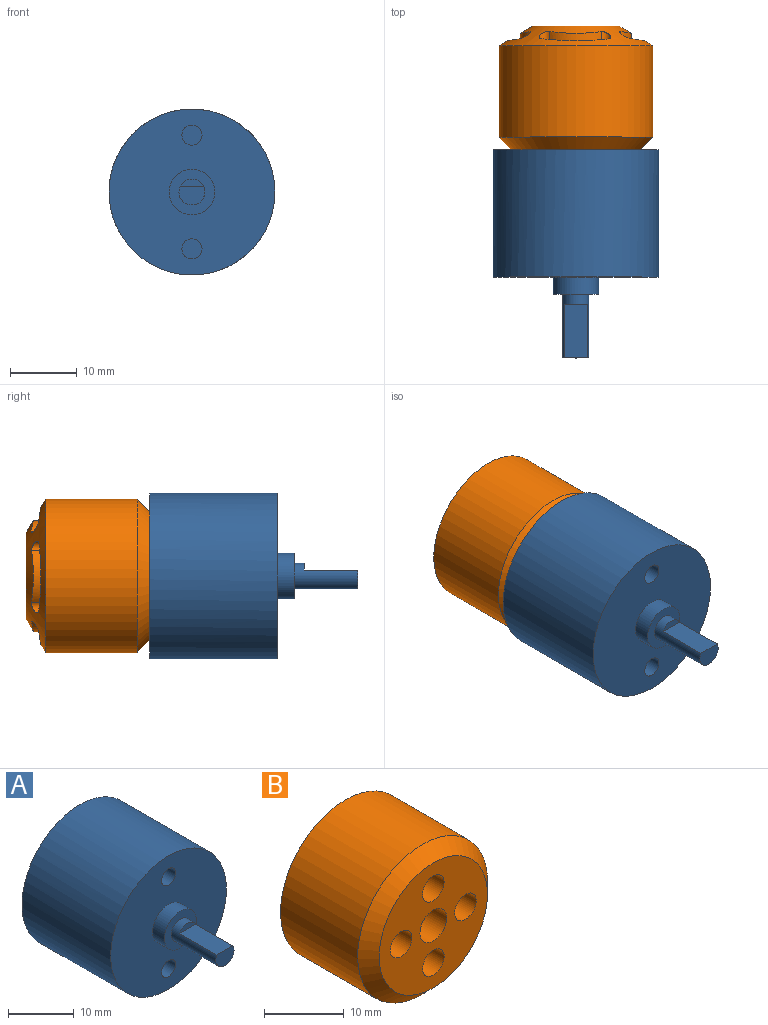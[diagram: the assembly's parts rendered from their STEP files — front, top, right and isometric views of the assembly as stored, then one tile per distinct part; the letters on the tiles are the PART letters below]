
ASSEMBLY  parts=2 mates=1
PART A: 15 faces, bbox 24.8x31.1x24.8 mm
  f0: cylinder r=12.4mm len=24.8mm, axis (0,-1,0), area 1481.6mm2, adj f2,f12
  f1: plane 6.83x6.83mm, normal (0,-1,0), area 24.8mm2, adj f3,f4
  f2: plane 24.8x24.8mm, normal (0,-1,0), area 432.3mm2, adj f0,f3,f8,f10
  f3: cylinder r=3.42mm len=6.83mm, axis (0,1,0), area 54.5mm2, adj f1,f2
  f4: cylinder r=1.94mm len=9.55mm, axis (0,1,0), area 82.5mm2, adj f1,f5,f6,f7
  f5: plane 3.88x2.84mm, normal (0,-1,0), area 9.3mm2, adj f4,f7
  f6: plane 3.44x1.05mm, normal (0,-1,0), area 2.6mm2, adj f4,f7
  f7: plane 8x3.44mm, normal (0,0,1), area 27.5mm2, adj f4,f5,f6
  f8: cylinder r=1.5mm len=4mm, axis (0,-1,0), area 37.7mm2, adj f2,f9
  f9: plane 3x3mm, normal (0,-1,0), area 7.1mm2, adj f8
  f10: cylinder r=1.5mm len=4mm, axis (0,-1,0), area 37.7mm2, adj f2,f11
  f11: plane 3x3mm, normal (0,-1,0), area 7.1mm2, adj f10
  f12: plane 24.8x24.8mm, normal (0,1,0), area 451.4mm2, adj f0,f13
  f13: cylinder r=3.17mm len=6.35mm, axis (0,1,0), area 51.2mm2, adj f12,f14
  f14: plane 6.35x6.35mm, normal (0,1,0), area 31.7mm2, adj f13
PART B: 35 faces, bbox 23x18.5x23 mm
  f0: plane 12.84x12.84mm, normal (0,1,0), area 129.5mm2, adj f24
  f1: cylinder r=11.5mm len=23mm, axis (0,-1,0), area 987.2mm2, adj f23,f24
  f2: plane 19.19x19.19mm, normal (0,-1,0), area 225.7mm2, adj f23,f25,f27,f29,f31,f33
  f3: cylinder r=0.99mm len=1.72mm, axis (0,1,0), area 3.2mm2, adj f4,f6,f7,f24
  f4: cylinder r=5.72mm len=7.74mm, axis (0,1,0), area 13.2mm2, adj f3,f5,f7,f24
  f5: cylinder r=0.97mm len=1.75mm, axis (0,1,0), area 3.6mm2, adj f4,f6,f7,f24
  f6: cylinder r=7.64mm len=10.34mm, axis (0,1,0), area 5.1mm2, adj f3,f5,f7,f24
  f7: plane 10.75x3.72mm, normal (0,1,0), area 21.4mm2, adj f3,f4,f5,f6
  f8: cylinder r=0.99mm len=1.72mm, axis (0,1,0), area 3.2mm2, adj f9,f11,f12,f24
  f9: cylinder r=5.72mm len=7.74mm, axis (0,1,0), area 13.2mm2, adj f8,f10,f12,f24
  f10: cylinder r=0.97mm len=1.75mm, axis (0,1,0), area 3.6mm2, adj f9,f11,f12,f24
  f11: cylinder r=7.64mm len=10.34mm, axis (0,1,0), area 5.1mm2, adj f8,f10,f12,f24
  f12: plane 10.75x3.72mm, normal (0,1,0), area 21.4mm2, adj f8,f9,f10,f11
  f13: cylinder r=0.99mm len=1.72mm, axis (0,1,0), area 3.2mm2, adj f14,f16,f17,f24
  f14: cylinder r=5.72mm len=7.74mm, axis (0,1,0), area 13.2mm2, adj f13,f15,f17,f24
  f15: cylinder r=0.97mm len=1.75mm, axis (0,1,0), area 3.6mm2, adj f14,f16,f17,f24
  f16: cylinder r=7.64mm len=10.34mm, axis (0,1,0), area 5.1mm2, adj f13,f15,f17,f24
  f17: plane 10.75x3.72mm, normal (0,1,0), area 21.4mm2, adj f13,f14,f15,f16
  f18: cylinder r=0.99mm len=1.72mm, axis (0,1,0), area 3.2mm2, adj f19,f21,f22,f24
  f19: cylinder r=5.72mm len=7.74mm, axis (0,1,0), area 13.2mm2, adj f18,f20,f22,f24
  f20: cylinder r=0.97mm len=1.75mm, axis (0,1,0), area 3.6mm2, adj f19,f21,f22,f24
  f21: cylinder r=7.64mm len=10.34mm, axis (0,1,0), area 5.1mm2, adj f18,f20,f22,f24
  f22: plane 10.75x3.72mm, normal (0,1,0), area 21.4mm2, adj f18,f19,f20,f21
  f23: cone r=11.5mm half-angle=45deg, axis (0,1,0), area 178.5mm2, adj f1,f2
  f24: cone r=6.42mm half-angle=60deg, axis (0,-1,0), area 231.3mm2, adj f0,f1,f3,f4,f5,f6,f8,f9
  f25: cylinder r=2.37mm len=4.74mm, axis (0,-1,0), area 56.7mm2, adj f2,f26
  f26: plane 4.74x4.74mm, normal (0,-1,0), area 17.6mm2, adj f25
  f27: cylinder r=1.91mm len=3.82mm, axis (0,-1,0), area 45.8mm2, adj f2,f28
  f28: plane 3.82x3.82mm, normal (0,-1,0), area 11.5mm2, adj f27
  f29: cylinder r=1.91mm len=3.82mm, axis (0,-1,0), area 45.8mm2, adj f2,f30
  f30: plane 3.82x3.82mm, normal (0,-1,0), area 11.5mm2, adj f29
  f31: cylinder r=1.91mm len=3.82mm, axis (0,-1,0), area 45.8mm2, adj f2,f32
  f32: plane 3.82x3.82mm, normal (0,-1,0), area 11.5mm2, adj f31
  f33: cylinder r=1.91mm len=3.82mm, axis (0,-1,0), area 45.8mm2, adj f2,f34
  f34: plane 3.82x3.82mm, normal (0,-1,0), area 11.5mm2, adj f33
PLACE A t=(-20.21,-19.85,-0.9)mm
PLACE B t=(-20.21,-19.85,-0.9)mm
MATE fastened A.f0 <-> B.f1  axis (0,1,0) through (-20.21,-0.84,-0.9)mm
